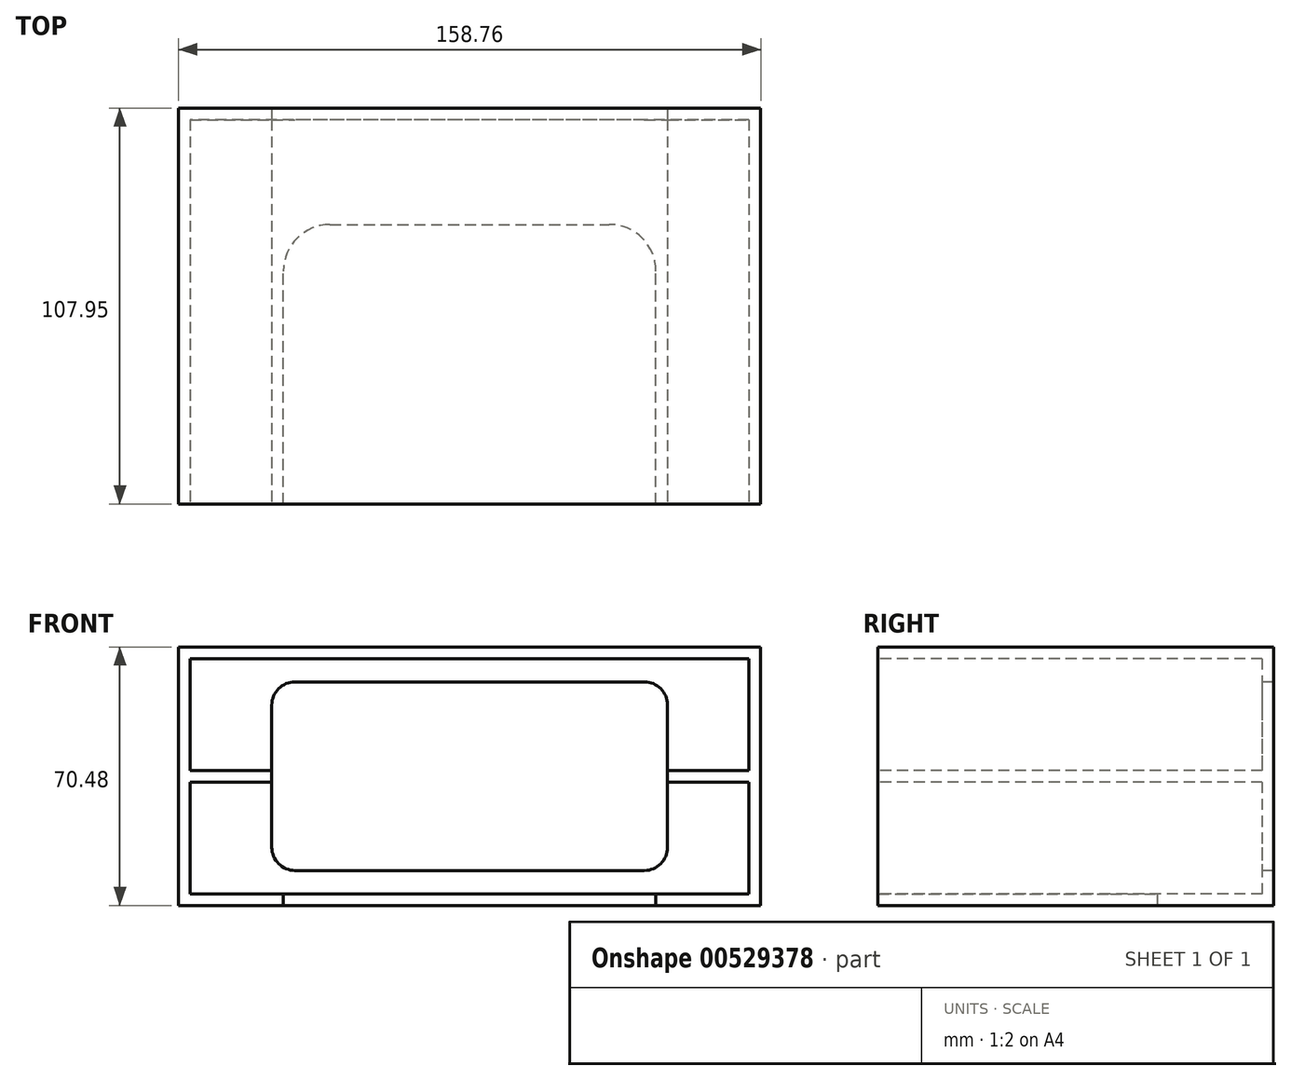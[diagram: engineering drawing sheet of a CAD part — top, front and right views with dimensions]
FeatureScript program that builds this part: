
annotation { "Feature Type Name" : "Feature", "Feature Type Description" : "" }
export const myFeature = defineFeature(function(context is Context, id is Id, definition is map)
    precondition{}
    {
        {
            var Q0;
            Q0=qCreatedBy(makeId("Front.planeOp"),FACE);
            var sketch = newSketch(context, id + "F0", { "sketchPlane" : qUnion([Q0])});
            skLineSegment(sketch, "E0.bottom", {"start": v(-79.37, -35.24) * mm, "end": v(79.38, -35.24) * mm});
            skLineSegment(sketch, "E0.top", {"start": v(-79.38, 35.24) * mm, "end": v(79.37, 35.24) * mm});
            skLineSegment(sketch, "E0.left", {"start": v(-79.37, -35.24) * mm, "end": v(-79.38, 35.24) * mm});
            skLineSegment(sketch, "E0.right", {"start": v(79.38, -35.24) * mm, "end": v(79.37, 35.24) * mm});
            skPoint(sketch, "E0.middle", {"position": v(0, 0) * mm});
            skSolve(sketch);
        }
        {
            var Q0;
            Q0 = qSketchRegion(id + "F0", true);
            extrude(context, id + "F1", {"entities" : qUnion([Q0]), "oppositeDirection" : true, "depth" : 104.77 * mm, "offsetDistance" : 25.4 * mm});
        }
        {
            var Q0;
            Q0=makeQuery(id+"F1.opExtrude","CAP_FACE",FACE,{"disambiguationData":[OSD([sQuery(id+"F0.wireOp",EDGE,"E0.bottom"),sQuery(id+"F0.wireOp",EDGE,"E0.top"),sQuery(id+"F0.wireOp",EDGE,"E0.left"),sQuery(id+"F0.wireOp",EDGE,"E0.right")])],"isStart":true});
            shell(context, id + "F2", {"entities" : qUnion([Q0]), "thickness" : 3.17 * mm});
        }
        {
            var Q0;
            Q0=makeQuery(id+"F2.opShell","OFFSET_FACE",FACE,{"disambiguationData":[OSD([sQuery(id+"F0.wireOp",EDGE,"E0.bottom"),sQuery(id+"F0.wireOp",EDGE,"E0.top"),sQuery(id+"F0.wireOp",EDGE,"E0.left"),sQuery(id+"F0.wireOp",EDGE,"E0.right")])]});
            var sketch = newSketch(context, id + "F3", { "sketchPlane" : qUnion([Q0])});
            skLineSegment(sketch, "E1.bottom", {"start": v(-76.2, -32.07) * mm, "end": v(76.2, -32.07) * mm});
            skLineSegment(sketch, "E1.top", {"start": v(-76.2, 32.07) * mm, "end": v(76.2, 32.07) * mm});
            skLineSegment(sketch, "E1.left", {"start": v(-76.2, -32.07) * mm, "end": v(-76.2, 32.07) * mm});
            skLineSegment(sketch, "E1.right", {"start": v(76.2, -32.07) * mm, "end": v(76.2, 32.07) * mm});
            skPoint(sketch, "E1.middle", {"position": v(0, 0) * mm});
            skSolve(sketch);
        }
        {
            var Q0;
            Q0 = qSketchRegion(id + "F3", true);
            extrude(context, id + "F4", {"entities" : qUnion([Q0]), "operationType" : NewBodyOperationType.REMOVE, "endBound" : BoundingType.UP_TO_NEXT, "oppositeDirection" : true, "depth" : 25.4 * mm, "offsetDistance" : 25.4 * mm});
        }
        {
            var Q0;
            Q0=makeQuery(id+"F1.opExtrude","CAP_FACE",FACE,{"disambiguationData":[OSD([sQuery(id+"F0.wireOp",EDGE,"E0.bottom"),sQuery(id+"F0.wireOp",EDGE,"E0.top"),sQuery(id+"F0.wireOp",EDGE,"E0.left"),sQuery(id+"F0.wireOp",EDGE,"E0.right")])],"isStart":true});
            var sketch = newSketch(context, id + "F5", { "sketchPlane" : qUnion([Q0])});
            skLineSegment(sketch, "E2.bottom", {"start": v(-76.2, -1.59) * mm, "end": v(76.2, -1.59) * mm});
            skLineSegment(sketch, "E2.top", {"start": v(-76.2, 1.59) * mm, "end": v(76.2, 1.59) * mm});
            skLineSegment(sketch, "E2.left", {"start": v(-76.2, -1.59) * mm, "end": v(-76.2, 1.59) * mm});
            skLineSegment(sketch, "E2.right", {"start": v(76.2, -1.59) * mm, "end": v(76.2, 1.59) * mm});
            skPoint(sketch, "E2.middle", {"position": v(0, 0) * mm});
            skSolve(sketch);
        }
        {
            var Q0;
            Q0=makeQuery(id+"F5.imprint","IMPRINT",FACE,{"disambiguationData":[TD([[makeQuery(id+"F5.imprint","IMPRINT",EDGE,{"derivedFrom":sQuery(id+"F5.wireOp",EDGE,"E2.bottom")}),1.0]])]});
            extrude(context, id + "F6", {"entities" : qUnion([Q0]), "operationType" : NewBodyOperationType.ADD, "oppositeDirection" : true, "depth" : 104.77 * mm, "offsetDistance" : 25.4 * mm});
        }
        {
            var Q0;
            Q0=makeQuery(id+"F6.boolean.opBoolean","MERGE",FACE,{"derivedFrom":[makeQuery(id+"F1.opExtrude","CAP_FACE",FACE,{"disambiguationData":[OSD([sQuery(id+"F0.wireOp",EDGE,"E0.bottom"),sQuery(id+"F0.wireOp",EDGE,"E0.top"),sQuery(id+"F0.wireOp",EDGE,"E0.left"),sQuery(id+"F0.wireOp",EDGE,"E0.right")])],"isStart":true}),makeQuery(id+"F6.opExtrude","CAP_FACE",FACE,{"disambiguationData":[OSD([sQuery(id+"F5.wireOp",EDGE,"E2.bottom"),sQuery(id+"F5.wireOp",EDGE,"E2.top"),sQuery(id+"F5.wireOp",EDGE,"E2.left"),sQuery(id+"F5.wireOp",EDGE,"E2.right")])],"isStart":true})]});
            var sketch = newSketch(context, id + "F7", { "sketchPlane" : qUnion([Q0])});
            skLineSegment(sketch, "E3.bottom", {"start": v(53.98, -1.59) * mm, "end": v(-53.98, -1.59) * mm});
            skLineSegment(sketch, "E3.top", {"start": v(53.98, 1.59) * mm, "end": v(-53.98, 1.59) * mm});
            skLineSegment(sketch, "E3.left", {"start": v(53.98, -1.59) * mm, "end": v(53.98, 1.59) * mm});
            skLineSegment(sketch, "E3.right", {"start": v(-53.98, -1.59) * mm, "end": v(-53.98, 1.59) * mm});
            skPoint(sketch, "E3.middle", {"position": v(0, 0) * mm});
            skSolve(sketch);
        }
        {
            var Q0;
            Q0 = qSketchRegion(id + "F7", true);
            extrude(context, id + "F8", {"entities" : qUnion([Q0]), "operationType" : NewBodyOperationType.REMOVE, "endBound" : BoundingType.UP_TO_NEXT, "oppositeDirection" : true, "depth" : 25.4 * mm, "offsetDistance" : 25.4 * mm});
        }
        {
            var Q0;
            Q0=makeQuery(id+"F6.boolean.opBoolean","MERGE",FACE,{"derivedFrom":[makeQuery(id+"F1.opExtrude","CAP_FACE",FACE,{"disambiguationData":[OSD([sQuery(id+"F0.wireOp",EDGE,"E0.bottom"),sQuery(id+"F0.wireOp",EDGE,"E0.top"),sQuery(id+"F0.wireOp",EDGE,"E0.left"),sQuery(id+"F0.wireOp",EDGE,"E0.right")])],"isStart":false}),makeQuery(id+"F6.opExtrude","CAP_FACE",FACE,{"disambiguationData":[OSD([sQuery(id+"F5.wireOp",EDGE,"E2.bottom"),sQuery(id+"F5.wireOp",EDGE,"E2.top"),sQuery(id+"F5.wireOp",EDGE,"E2.left"),sQuery(id+"F5.wireOp",EDGE,"E2.right")])],"isStart":false})]});
            var sketch = newSketch(context, id + "F9", { "sketchPlane" : qUnion([Q0])});
            skLineSegment(sketch, "E4.bottom", {"start": v(79.37, -35.24) * mm, "end": v(-79.37, -35.24) * mm});
            skLineSegment(sketch, "E4.top", {"start": v(79.37, 35.24) * mm, "end": v(-79.37, 35.24) * mm});
            skLineSegment(sketch, "E4.left", {"start": v(79.37, -35.24) * mm, "end": v(79.37, 35.24) * mm});
            skLineSegment(sketch, "E4.right", {"start": v(-79.37, -35.24) * mm, "end": v(-79.37, 35.24) * mm});
            skPoint(sketch, "E4.middle", {"position": v(0, 0) * mm});
            skLineSegment(sketch, "E5.bottom", {"start": v(-53.98, 25.72) * mm, "end": v(53.98, 25.72) * mm});
            skLineSegment(sketch, "E5.top", {"start": v(-53.98, -25.72) * mm, "end": v(53.98, -25.72) * mm});
            skLineSegment(sketch, "E5.left", {"start": v(-53.98, 25.72) * mm, "end": v(-53.98, -25.72) * mm});
            skLineSegment(sketch, "E5.right", {"start": v(53.98, 25.72) * mm, "end": v(53.98, -25.72) * mm});
            skSolve(sketch);
        }
        {
            var Q0;
            Q0 = qSketchRegion(id + "F9", true);
            extrude(context, id + "F10", {"entities" : qUnion([Q0]), "operationType" : NewBodyOperationType.ADD, "depth" : 3.17 * mm, "offsetDistance" : 25.4 * mm});
        }
        {
            var Q0;
            Q0=makeQuery(id+"F10.opExtrude","SWEPT_EDGE",EDGE,{"disambiguationData":[OSD([sQuery(id+"F9.wireOp",EDGE,"E5.bottom"),sQuery(id+"F9.wireOp",EDGE,"E5.left")])]});
            var Q1;
            Q1=makeQuery(id+"F10.opExtrude","SWEPT_EDGE",EDGE,{"disambiguationData":[OSD([sQuery(id+"F9.wireOp",EDGE,"E5.bottom"),sQuery(id+"F9.wireOp",EDGE,"E5.right")])]});
            var Q2;
            Q2=makeQuery(id+"F10.opExtrude","SWEPT_EDGE",EDGE,{"disambiguationData":[OSD([sQuery(id+"F9.wireOp",EDGE,"E5.top"),sQuery(id+"F9.wireOp",EDGE,"E5.right")])]});
            var Q3;
            Q3=makeQuery(id+"F10.opExtrude","SWEPT_EDGE",EDGE,{"disambiguationData":[OSD([sQuery(id+"F9.wireOp",EDGE,"E5.top"),sQuery(id+"F9.wireOp",EDGE,"E5.left")])]});
            fillet(context, id + "F11", {"entities" : qUnion([Q0, Q1, Q2, Q3]), "radius" : 6.35 * mm, "tangentPropagation" : true, "allowEdgeOverflow" : false});
        }
        {
            var Q0;
            Q0=makeQuery(id+"F10.boolean.opBoolean","MERGE",FACE,{"derivedFrom":[makeQuery(id+"F1.opExtrude","SWEPT_FACE",FACE,{"disambiguationData":[OSD([sQuery(id+"F0.wireOp",EDGE,"E0.bottom")])]}),makeQuery(id+"F10.opExtrude","SWEPT_FACE",FACE,{"disambiguationData":[OSD([sQuery(id+"F9.wireOp",EDGE,"E4.bottom")])]})]});
            var sketch = newSketch(context, id + "F12", { "sketchPlane" : qUnion([Q0])});
            skLineSegment(sketch, "E6.bottom", {"start": v(50.8, -76.2) * mm, "end": v(-50.8, -76.2) * mm});
            skLineSegment(sketch, "E6.top", {"start": v(50.8, 76.2) * mm, "end": v(-50.8, 76.2) * mm});
            skLineSegment(sketch, "E6.left", {"start": v(50.8, -76.2) * mm, "end": v(50.8, 76.2) * mm});
            skLineSegment(sketch, "E6.right", {"start": v(-50.8, -76.2) * mm, "end": v(-50.8, 76.2) * mm});
            skPoint(sketch, "E6.middle", {"position": v(0, 0) * mm});
            skSolve(sketch);
        }
        {
            var Q0;
            {var subQ0=sQuery(id+"F12.wireOp",EDGE,"E6.bottom");Q0=makeQuery(id+"F12.imprint","IMPRINT",FACE,{"disambiguationData":[TD([[makeQuery(id+"F12.imprint","IMPRINT",EDGE,{"derivedFrom":subQ0}),-1.0]])]});}
            extrude(context, id + "F13", {"entities" : qUnion([Q0]), "operationType" : NewBodyOperationType.REMOVE, "endBound" : BoundingType.UP_TO_NEXT, "oppositeDirection" : true, "depth" : 25.4 * mm, "offsetDistance" : 25.4 * mm});
        }
        {
            var Q0;
            Q0=makeQuery(id+"F13.boolean.opBoolean","COPY",EDGE,{"derivedFrom":makeQuery(id+"F13.opExtrude","SWEPT_EDGE",EDGE,{"disambiguationData":[OSD([sQuery(id+"F12.wireOp",EDGE,"E6.bottom"),sQuery(id+"F12.wireOp",EDGE,"E6.right")])]})});
            var Q1;
            Q1=makeQuery(id+"F13.boolean.opBoolean","COPY",EDGE,{"derivedFrom":makeQuery(id+"F13.opExtrude","SWEPT_EDGE",EDGE,{"disambiguationData":[OSD([sQuery(id+"F12.wireOp",EDGE,"E6.bottom"),sQuery(id+"F12.wireOp",EDGE,"E6.left")])]})});
            fillet(context, id + "F14", {"entities" : qUnion([Q0, Q1]), "radius" : 12.7 * mm, "tangentPropagation" : true, "allowEdgeOverflow" : false});
        }
    });
